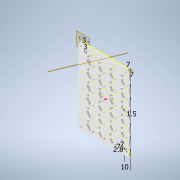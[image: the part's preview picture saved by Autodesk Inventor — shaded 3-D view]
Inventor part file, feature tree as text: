
AUTODESK INVENTOR PART (.ipt)
format: ipt  version: 2022 (Build 260153000, 153)  size: 423,936 bytes
history: native  units: mm
features: sketch x5, plane x4, extrude x4, reference x3, other x2, mirror x1, pattern_linear x1, projected_geometry x1
ambient origin geometry x8: Origin, YZ Plane, XZ Plane, XY Plane, X Axis, Y Axis, Z Axis, Center Point
bodies: Volumenkörper1 (feature_tree)
feature tree (21):
  plane  "Arbeitsebene4"
  sketch  "Skizze1"  dims[d0=1.5mm d1=3.0mm]
  plane  "Arbeitsebene2"
  plane  "Arbeitsebene6"
  extrude  "Extrusion2"  Depth=3.0mm
  extrude  "Extrusion3"  Depth=3.0mm
  extrude  "Extrusion4"  Depth=7.0mm
  extrude  "Extrusion5"  Depth=10.0mm
  plane  "Arbeitsebene7"
  mirror  "Spiegeln1"
  pattern_linear  "Rechteckige Anordnung3"  Spacing1=3.0mm  [1 undecoded]
  sketch  "Skizze2"  dims[d2=3.0mm d5=7.0mm]
  projected_geometry  "Projizierte Kontur1"
  sketch  "Skizze3"  dims[d6=7.0mm d7=7.0mm]
  sketch  "Skizze4"  dims[d8=7.0mm d9=10.0mm]
  sketch  "Skizze5"  dims[d10=2.8mm d11=3.0mm d12=0.0mm d15=21.816616mm d19=9.0mm d20=6.0mm d21=55.0mm d22=0.0mm d35=9.0mm d36=1.0mm d37=0.0mm d40=2.5mm d41=2.7mm d42=0.3mm d43=0.0mm d44=0.0mm d45=60.0mm d47=18.9mm d48=40.0mm d50=18.9mm d51=0.3mm d52=0.3mm]
  reference  "Referenz5"
  reference  "Referenz6"
  reference  "Referenz7"
  other  "Omniscope_new_v0.iam"
  other  "Omniscope_Camera_fix:1"
note: 1 required parameter value undecoded (feature->parameter linkage not recoverable at this tier; creation-order binding heuristic only, values carry confidence <= 0.55)
